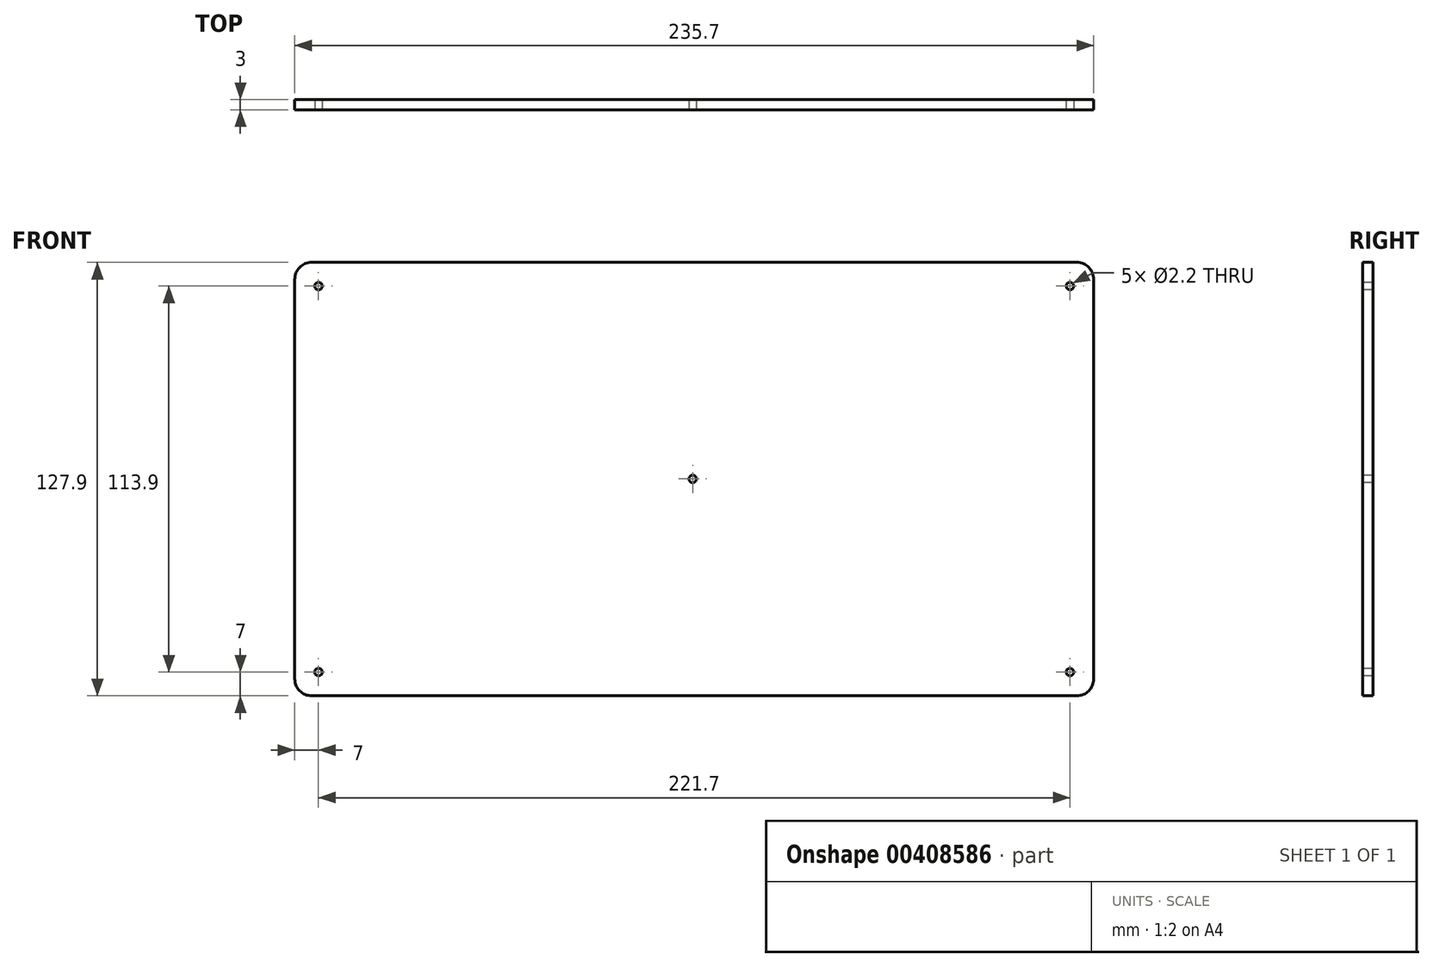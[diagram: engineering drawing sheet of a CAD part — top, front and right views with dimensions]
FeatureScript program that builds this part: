
annotation { "Feature Type Name" : "Feature", "Feature Type Description" : "" }
export const myFeature = defineFeature(function(context is Context, id is Id, definition is map)
    precondition{}
    {
        {
            var Q0;
            Q0=qCreatedBy(makeId("Front.planeOp"),FACE);
            var sketch = newSketch(context, id + "F0", { "sketchPlane" : qUnion([Q0])});
            skLineSegment(sketch, "E0.bottom", {"start": v(5, 0) * mm, "end": v(230.7, 0) * mm});
            skLineSegment(sketch, "E0.top", {"start": v(5, 127.9) * mm, "end": v(230.7, 127.9) * mm});
            skLineSegment(sketch, "E0.left", {"start": v(0, 5) * mm, "end": v(0, 122.9) * mm});
            skLineSegment(sketch, "E0.right", {"start": v(235.7, 5) * mm, "end": v(235.7, 122.9) * mm});
            skPoint(sketch, "E1.visualSharp", {"position": v(0, 127.9) * mm});
            skArc(sketch, "E1.filletArc", {"start": v(5, 127.9) * mm, "mid": v(1.46, 126.44) * mm, "end": v(0, 122.9) * mm});
            skPoint(sketch, "E2.visualSharp", {"position": v(235.7, 127.9) * mm});
            skArc(sketch, "E2.filletArc", {"start": v(235.7, 122.9) * mm, "mid": v(234.24, 126.44) * mm, "end": v(230.7, 127.9) * mm});
            skPoint(sketch, "E3.visualSharp", {"position": v(235.7, 0) * mm});
            skArc(sketch, "E3.filletArc", {"start": v(230.7, 0) * mm, "mid": v(234.24, 1.46) * mm, "end": v(235.7, 5) * mm});
            skPoint(sketch, "E4.visualSharp", {"position": v(0, 0) * mm});
            skArc(sketch, "E4.filletArc", {"start": v(0, 5) * mm, "mid": v(1.46, 1.46) * mm, "end": v(5, 0) * mm});
            skSolve(sketch);
        }
        {
            var Q0;
            Q0 = qSketchRegion(id + "F0", true);
            extrude(context, id + "F1", {"entities" : qUnion([Q0]), "depth" : 3 * mm});
        }
        {
            var Q0;
            Q0=makeQuery(id+"F1.opExtrude","CAP_FACE",FACE,{"disambiguationData":[OSD([sQuery(id+"F0.wireOp",EDGE,"E0.bottom"),sQuery(id+"F0.wireOp",EDGE,"E0.top"),sQuery(id+"F0.wireOp",EDGE,"E0.left"),sQuery(id+"F0.wireOp",EDGE,"E0.right"),sQuery(id+"F0.wireOp",EDGE,"E1.filletArc"),sQuery(id+"F0.wireOp",EDGE,"E2.filletArc"),sQuery(id+"F0.wireOp",EDGE,"E3.filletArc"),sQuery(id+"F0.wireOp",EDGE,"E4.filletArc")])],"isStart":false});
            var sketch = newSketch(context, id + "F2", { "sketchPlane" : qUnion([Q0])});
            skCircle(sketch, "E5", {"center": v(7, 7) * mm, "radius": 1.1 * mm});
            skCircle(sketch, "E6", {"center": v(7, 120.9) * mm, "radius": 1.1 * mm});
            skCircle(sketch, "E7", {"center": v(228.7, 120.9) * mm, "radius": 1.1 * mm});
            skCircle(sketch, "E8", {"center": v(228.7, 7) * mm, "radius": 1.1 * mm});
            skCircle(sketch, "E9", {"center": v(117.4, 64) * mm, "radius": 1.1 * mm});
            skSolve(sketch);
        }
        {
            var Q0;
            Q0 = qSketchRegion(id + "F2", true);
            extrude(context, id + "F3", {"entities" : qUnion([Q0]), "operationType" : NewBodyOperationType.REMOVE, "endBound" : BoundingType.THROUGH_ALL, "oppositeDirection" : true, "depth" : 25 * mm});
        }
    });
